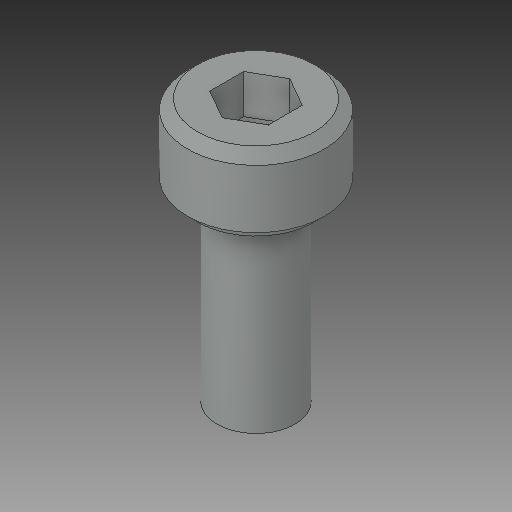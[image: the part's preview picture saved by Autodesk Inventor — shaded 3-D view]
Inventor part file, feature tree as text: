
AUTODESK INVENTOR PART (.ipt)
format: ipt  version: 2017 (Build 210142000, 142)  size: 106,496 bytes
history: native  units: in
note: dims shown in document units (in); Inventor stores cm internally (conversion verified against a paired STEP export)
features: chamfer x1
ambient origin geometry x8: Origin, YZ Plane, XZ Plane, XY Plane, X Axis, Y Axis, Z Axis, Center Point
bodies: Solid1 (feature_tree)
feature tree (1):
  chamfer  "Chamfer2"  [1 undecoded]
note: 1 required parameter value undecoded (feature->parameter linkage not recoverable at this tier; creation-order binding heuristic only, values carry confidence <= 0.55)
